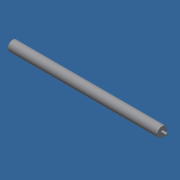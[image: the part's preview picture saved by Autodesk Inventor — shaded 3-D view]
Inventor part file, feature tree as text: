
AUTODESK INVENTOR PART (.ipt)
format: ipt  version: 2018 (Build 220112000, 112)  size: 78,336 bytes
history: native  units: mm
features: other x1, extrude x1, sketch x1
ambient origin geometry x8: Origin, YZ Plane, XZ Plane, XY Plane, X Axis, Y Axis, Z Axis, Center Point
bodies: Solid1 (feature_tree)
feature tree (3):
  other  "<userpath>\OneDrive\Objet3D\3DPrinter\Parameters.xlsx"
  extrude  "Extrusion1"  Depth=300.0mm TaperAngle=0.0deg
  sketch  "Sketch1"  dims[d0=20.0mm d1=300.0mm d2=0.0mm d6=18.0mm]
